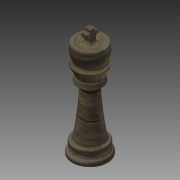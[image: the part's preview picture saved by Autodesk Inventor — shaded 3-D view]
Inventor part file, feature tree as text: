
AUTODESK INVENTOR PART (.ipt)
format: ipt  version: 2015 SP1 (Build 190203100, 203)  size: 566,784 bytes
history: native  units: mm
features: fillet x4, sketch x2, revolve x1, extrude x1
ambient origin geometry x8: Origin, YZ Plane, XZ Plane, XY Plane, X Axis, Y Axis, Z Axis, Center Point
bodies: Body1 (feature_tree)
feature tree (8):
  revolve  "Revolution2"  [1 undecoded]
  fillet  "Fillet6"  Radius=2.0mm
  fillet  "Fillet7"  [1 undecoded]
  extrude  "Extrusion3"  Depth=0.5mm
  fillet  "Fillet8"  Radius=10.0mm
  fillet  "Fillet9"  Radius=2.0mm
  sketch  "Sketch1"  dims[d11=2.0mm d13=1.0mm d24=2.0mm d40=90.0deg]
  sketch  "Sketch4"  dims[d41=2.0mm d42=2.0mm d45=10.0mm d46=2.0mm d47=2.5mm d48=3.0mm d49=3.0mm d50=5.0mm d51=0.0mm d52=2.0mm d53=0.5mm]
note: 2 required parameter values undecoded (feature->parameter linkage not recoverable at this tier; creation-order binding heuristic only, values carry confidence <= 0.55)